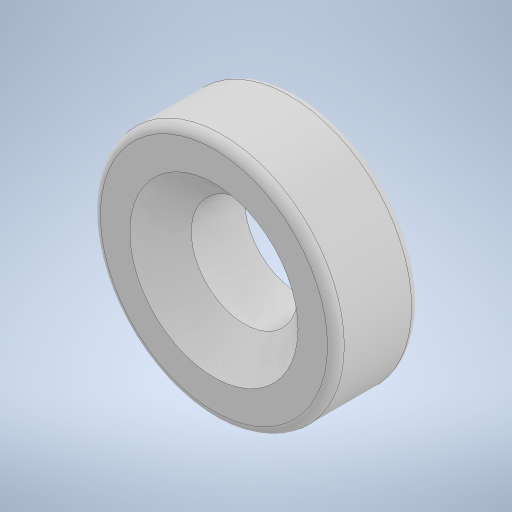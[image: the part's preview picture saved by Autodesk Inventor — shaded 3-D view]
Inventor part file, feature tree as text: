
AUTODESK INVENTOR PART (.ipt)
format: ipt  version: 2023 (Build 270158000, 158)  size: 257,536 bytes
history: native  units: mm
features: sketch x1, extrude x1, hole x1, fillet x1
ambient origin geometry x8: Origin, YZ Plane, XZ Plane, XY Plane, X Axis, Y Axis, Z Axis, Center Point
bodies: Solid1 (feature_tree)
feature tree (4):
  sketch  "Sketch1"  dims[d0=14.5mm d2=5.0mm d3=0.0mm d4=6.35mm d5=6.0mm d6=10.0mm d7=2.0mm d8=90.0deg d9=8.0mm d10=20.594885mm d11=0.5mm]
  extrude  "Extrusion1"  Depth=5.0mm TaperAngle=0.0deg
  hole  "Hole1"  [1 undecoded]
  fillet  "Fillet1"  [1 undecoded]
note: 2 required parameter values undecoded (feature->parameter linkage not recoverable at this tier; creation-order binding heuristic only, values carry confidence <= 0.55)
